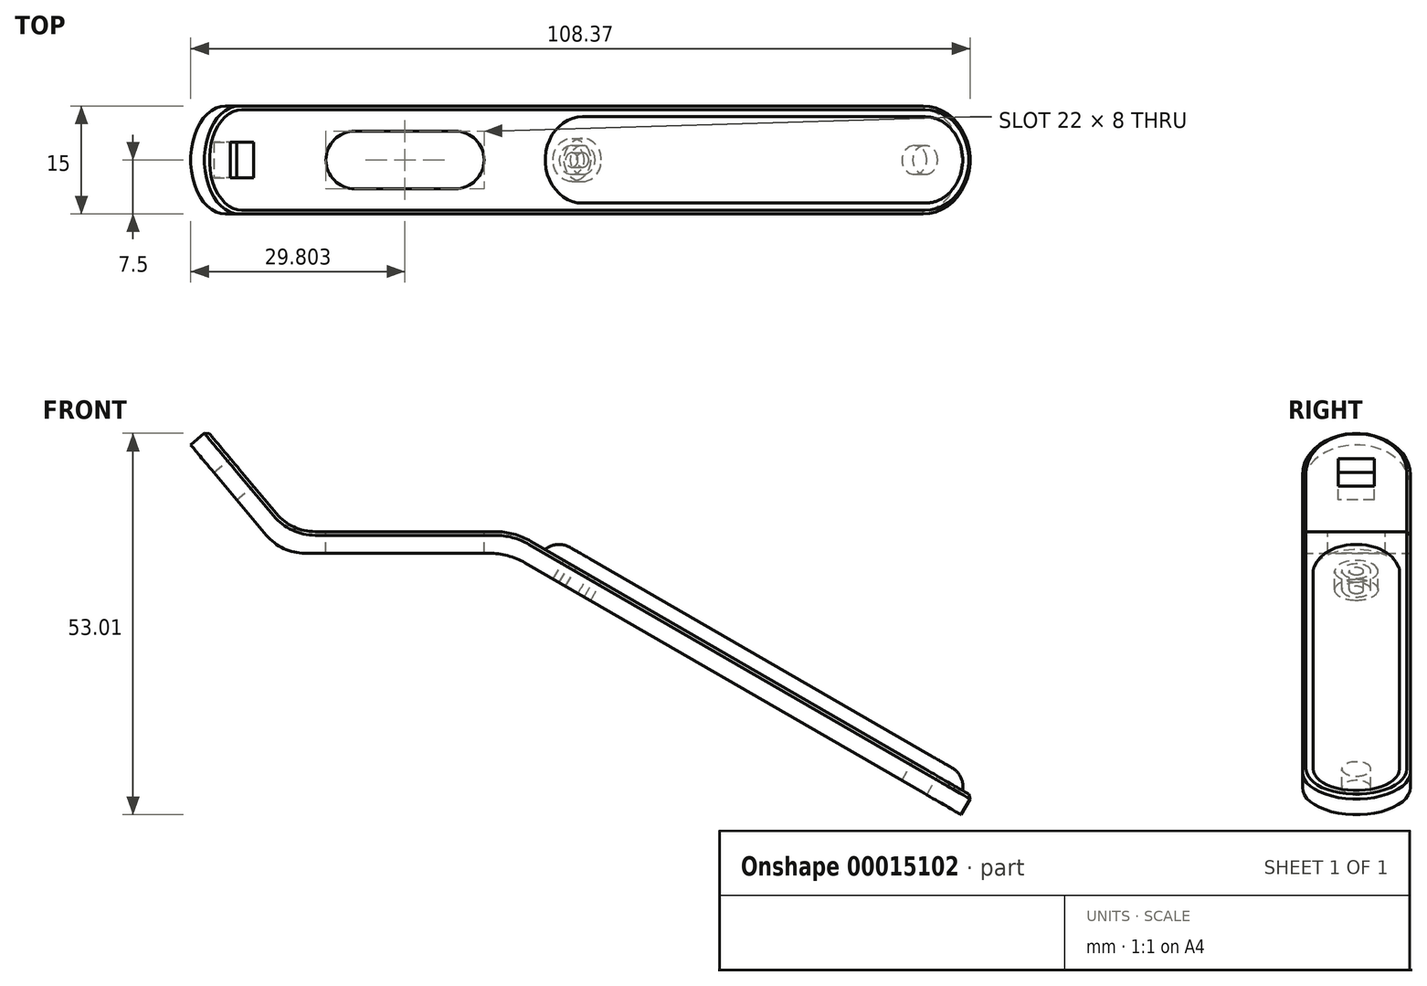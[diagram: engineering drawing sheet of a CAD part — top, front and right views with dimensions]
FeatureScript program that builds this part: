
annotation { "Feature Type Name" : "Feature", "Feature Type Description" : "" }
export const myFeature = defineFeature(function(context is Context, id is Id, definition is map)
    precondition{}
    {
        {
            var Q0;
            Q0=qCreatedBy(makeId("Front.planeOp"),FACE);
            var sketch = newSketch(context, id + "F0", { "sketchPlane" : qUnion([Q0])});
            skLineSegment(sketch, "E0.bottom", {"start": v(3.26, 0) * mm, "end": v(28.86, 0) * mm});
            skLineSegment(sketch, "E0.top", {"start": v(4.66, 3) * mm, "end": v(29.66, 3) * mm});
            skLineSegment(sketch, "E1", {"start": v(-0.7, 5.5) * mm, "end": v(-10.34, 17) * mm});
            skLineSegment(sketch, "E2", {"start": v(-10.34, 17) * mm, "end": v(-12.64, 15.06) * mm});
            skLineSegment(sketch, "E3", {"start": v(-12.64, 15.06) * mm, "end": v(-2.1, 2.5) * mm});
            skLineSegment(sketch, "E4", {"start": v(34.66, 1.66) * mm, "end": v(95.98, -33.74) * mm});
            skLineSegment(sketch, "E5", {"start": v(95.98, -33.74) * mm, "end": v(94.48, -36.34) * mm});
            skLineSegment(sketch, "E6", {"start": v(94.48, -36.34) * mm, "end": v(33.86, -1.34) * mm});
            skPoint(sketch, "E7.visualSharp", {"position": v(1.4, 3) * mm});
            skArc(sketch, "E7.filletArc", {"start": v(-0.7, 5.5) * mm, "mid": v(1.7, 3.66) * mm, "end": v(4.66, 3) * mm});
            skPoint(sketch, "E8.visualSharp", {"position": v(31.54, 0) * mm});
            skArc(sketch, "E8.filletArc", {"start": v(33.86, -1.34) * mm, "mid": v(31.45, -0.34) * mm, "end": v(28.86, 0) * mm});
            skPoint(sketch, "E9.visualSharp", {"position": v(32.34, 3) * mm});
            skArc(sketch, "E9.filletArc", {"start": v(34.66, 1.66) * mm, "mid": v(32.25, 2.66) * mm, "end": v(29.66, 3) * mm});
            skPoint(sketch, "E10.visualSharp", {"position": v(0, 0) * mm});
            skArc(sketch, "E10.filletArc", {"start": v(-2.1, 2.5) * mm, "mid": v(0.3, 0.66) * mm, "end": v(3.26, 0) * mm});
            skSolve(sketch);
        }
        {
            var Q0;
            Q0=makeQuery(id+"F0.imprint","IMPRINT",FACE,{"disambiguationData":[TD([[makeQuery(id+"F0.imprint","IMPRINT",EDGE,{"derivedFrom":sQuery(id+"F0.wireOp",EDGE,"E0.bottom")}),1.0]])]});
            extrude(context, id + "F1", {"entities" : qUnion([Q0]), "endBound" : BoundingType.SYMMETRIC, "depth" : 15 * mm});
        }
        {
            var Q0;
            Q0=makeQuery(id+"F1.opExtrude","CAP_EDGE",EDGE,{"disambiguationData":[OSD([sQuery(id+"F0.wireOp",EDGE,"E2")])],"isStart":false});
            var Q1;
            Q1=makeQuery(id+"F1.opExtrude","CAP_EDGE",EDGE,{"disambiguationData":[OSD([sQuery(id+"F0.wireOp",EDGE,"E2")])],"isStart":true});
            var Q2;
            Q2=makeQuery(id+"F1.opExtrude","CAP_EDGE",EDGE,{"disambiguationData":[OSD([sQuery(id+"F0.wireOp",EDGE,"E5")])],"isStart":false});
            var Q3;
            Q3=makeQuery(id+"F1.opExtrude","CAP_EDGE",EDGE,{"disambiguationData":[OSD([sQuery(id+"F0.wireOp",EDGE,"E5")])],"isStart":true});
            fillet(context, id + "F2", {"entities" : qUnion([Q0, Q1, Q2, Q3]), "radius" : 7.5 * mm, "tangentPropagation" : true, "allowEdgeOverflow" : false});
        }
        {
            var Q0;
            Q0=makeQuery(id+"F1.opExtrude","SWEPT_FACE",FACE,{"disambiguationData":[OSD([sQuery(id+"F0.wireOp",EDGE,"E1")])]});
            var sketch = newSketch(context, id + "F3", { "sketchPlane" : qUnion([Q0])});
            skArc(sketch, "E11.0", {"start": v(7.5, 12.16) * mm, "mid": v(0, 19.66) * mm, "end": v(-7.5, 12.16) * mm});
            skLineSegment(sketch, "E12.rect.bottom", {"start": v(2.5, 9.66) * mm, "end": v(-2.5, 9.66) * mm});
            skLineSegment(sketch, "E12.rect.top", {"start": v(2.5, 14.66) * mm, "end": v(-2.5, 14.66) * mm});
            skLineSegment(sketch, "E12.rect.left", {"start": v(2.5, 9.66) * mm, "end": v(2.5, 14.66) * mm});
            skLineSegment(sketch, "E12.rect.right", {"start": v(-2.5, 9.66) * mm, "end": v(-2.5, 14.66) * mm});
            skSolve(sketch);
        }
        {
            var Q0;
            Q0=makeQuery(id+"F3.imprint","IMPRINT",FACE,{"disambiguationData":[TD([[makeQuery(id+"F3.imprint","IMPRINT",EDGE,{"derivedFrom":sQuery(id+"F3.wireOp",EDGE,"E12.rect.bottom")}),-1.0]])]});
            extrude(context, id + "F4", {"entities" : qUnion([Q0]), "operationType" : NewBodyOperationType.REMOVE, "endBound" : BoundingType.THROUGH_ALL, "oppositeDirection" : true, "depth" : 25 * mm});
        }
        {
            var Q0;
            Q0=makeQuery(id+"F1.opExtrude","SWEPT_FACE",FACE,{"disambiguationData":[OSD([sQuery(id+"F0.wireOp",EDGE,"E4")])]});
            var sketch = newSketch(context, id + "F5", { "sketchPlane" : qUnion([Q0])});
            skArc(sketch, "E13.0", {"start": v(92.5, -7.5) * mm, "mid": v(100, 0) * mm, "end": v(92.5, 7.5) * mm});
            skLineSegment(sketch, "E14", {"start": v(92.5, 0) * mm, "end": v(29.19, 0) * mm, "construction": true});
            skCircle(sketch, "E15", {"center": v(92.5, 0) * mm, "radius": 3 * mm});
            skCircle(sketch, "E16", {"center": v(37.5, 0) * mm, "radius": 3 * mm});
            skSolve(sketch);
        }
        {
            var Q0;
            Q0=makeQuery(id+"F5.imprint","IMPRINT",FACE,{"disambiguationData":[TD([[makeQuery(id+"F5.imprint","IMPRINT",EDGE,{"derivedFrom":sQuery(id+"F5.wireOp",EDGE,"E16")}),1.0]])]});
            var Q1;
            Q1=makeQuery(id+"F5.imprint","IMPRINT",FACE,{"disambiguationData":[TD([[makeQuery(id+"F5.imprint","IMPRINT",EDGE,{"derivedFrom":sQuery(id+"F5.wireOp",EDGE,"E15")}),1.0]])]});
            extrude(context, id + "F6", {"entities" : qUnion([Q0, Q1]), "operationType" : NewBodyOperationType.REMOVE, "endBound" : BoundingType.THROUGH_ALL, "oppositeDirection" : true, "depth" : 25 * mm});
        }
        {
            var Q0;
            Q0=makeQuery(id+"F1.opExtrude","SWEPT_FACE",FACE,{"disambiguationData":[OSD([sQuery(id+"F0.wireOp",EDGE,"E0.top")])]});
            var sketch = newSketch(context, id + "F7", { "sketchPlane" : qUnion([Q0])});
            skLineSegment(sketch, "E17", {"start": v(4.66, 0) * mm, "end": v(29.66, 0) * mm, "construction": true});
            skArc(sketch, "E18", {"start": v(10.16, 4) * mm, "mid": v(6.16, 0) * mm, "end": v(10.16, -4) * mm});
            skArc(sketch, "E19", {"start": v(24.16, -4) * mm, "mid": v(28.16, 0) * mm, "end": v(24.16, 4) * mm});
            skLineSegment(sketch, "E20", {"start": v(17.16, 7.5) * mm, "end": v(17.16, -7.5) * mm, "construction": true});
            skLineSegment(sketch, "E21", {"start": v(10.16, 4) * mm, "end": v(24.16, 4) * mm});
            skLineSegment(sketch, "E22", {"start": v(24.16, -4) * mm, "end": v(10.16, -4) * mm});
            skSolve(sketch);
        }
        {
            var Q0;
            Q0=makeQuery(id+"F7.imprint","IMPRINT",FACE,{"disambiguationData":[TD([[makeQuery(id+"F7.imprint","IMPRINT",EDGE,{"derivedFrom":sQuery(id+"F7.wireOp",EDGE,"E18")}),1.0]])]});
            extrude(context, id + "F8", {"entities" : qUnion([Q0]), "operationType" : NewBodyOperationType.REMOVE, "endBound" : BoundingType.THROUGH_ALL, "oppositeDirection" : true, "depth" : 25 * mm});
        }
        {
            var Q0;
            Q0=makeQuery(id+"F1.opExtrude","CAP_EDGE",EDGE,{"disambiguationData":[OSD([sQuery(id+"F0.wireOp",EDGE,"E1")])],"isStart":false});
            var Q1;
            Q1=makeQuery(id+"F2.opFillet","BLEND_EDGE",EDGE,{"blendedFrom":[makeQuery(id+"F1.opExtrude","CAP_EDGE",EDGE,{"disambiguationData":[OSD([sQuery(id+"F0.wireOp",EDGE,"E2")])],"isStart":false}),makeQuery(id+"F1.opExtrude","SWEPT_FACE",FACE,{"disambiguationData":[OSD([sQuery(id+"F0.wireOp",EDGE,"E3")])]})],"blendedInto":[makeQuery(id+"F1.opExtrude","SWEPT_FACE",FACE,{"disambiguationData":[OSD([sQuery(id+"F0.wireOp",EDGE,"E3")])]})]});
            chamfer(context, id + "F9", {"entities" : qUnion([Q0, Q1]), "width" : .5 * mm, "tangentPropagation" : true});
        }
        {
            var Q0;
            Q0=makeQuery(id+"F1.opExtrude","SWEPT_FACE",FACE,{"disambiguationData":[OSD([sQuery(id+"F0.wireOp",EDGE,"E4")])]});
            var sketch = newSketch(context, id + "F10", { "sketchPlane" : qUnion([Q0])});
            skCircle(sketch, "E23.0", {"center": v(37.5, 0) * mm, "radius": 3 * mm, "construction": true});
            skCircle(sketch, "E24.0", {"center": v(92.5, 0) * mm, "radius": 3 * mm});
            skCircle(sketch, "E25", {"center": v(37.5, 0) * mm, "radius": 2 * mm});
            skArc(sketch, "E26", {"start": v(92.5, -6) * mm, "mid": v(98.5, 0) * mm, "end": v(92.5, 6) * mm});
            skArc(sketch, "E27", {"start": v(37.5, 6) * mm, "mid": v(31.5, 0) * mm, "end": v(37.5, -6) * mm});
            skLineSegment(sketch, "E28", {"start": v(37.5, -6) * mm, "end": v(92.5, -6) * mm});
            skLineSegment(sketch, "E29", {"start": v(92.5, 6) * mm, "end": v(37.5, 6) * mm});
            skCircle(sketch, "E30", {"center": v(92.5, 0) * mm, "radius": 2 * mm});
            skCircle(sketch, "E31", {"center": v(37.5, 0) * mm, "radius": 1 * mm});
            skSolve(sketch);
        }
        {
            var Q0;
            Q0=makeQuery(id+"F10.imprint","IMPRINT",FACE,{"disambiguationData":[TD([[makeQuery(id+"F10.imprint","IMPRINT",EDGE,{"derivedFrom":sQuery(id+"F10.wireOp",EDGE,"E24.0")}),-1.0]])]});
            var Q1;
            Q1=makeQuery(id+"F10.imprint","IMPRINT",FACE,{"disambiguationData":[TD([[makeQuery(id+"F10.imprint","IMPRINT",EDGE,{"derivedFrom":sQuery(id+"F10.wireOp",EDGE,"E25")}),-1.0]])]});
            var Q2;
            Q2=makeQuery(id+"F10.imprint","IMPRINT",FACE,{"disambiguationData":[TD([[makeQuery(id+"F10.imprint","IMPRINT",EDGE,{"derivedFrom":sQuery(id+"F10.wireOp",EDGE,"E25")}),1.0]])]});
            var Q3;
            Q3=makeQuery(id+"F10.imprint","IMPRINT",FACE,{"disambiguationData":[TD([[makeQuery(id+"F10.imprint","IMPRINT",EDGE,{"derivedFrom":sQuery(id+"F10.wireOp",EDGE,"E31")}),1.0]])]});
            var Q4;
            Q4=makeQuery(id+"F10.imprint","IMPRINT",FACE,{"disambiguationData":[TD([[makeQuery(id+"F10.imprint","IMPRINT",EDGE,{"derivedFrom":sQuery(id+"F10.wireOp",EDGE,"E24.0")}),1.0]])]});
            var Q5;
            Q5=makeQuery(id+"F10.imprint","IMPRINT",FACE,{"disambiguationData":[TD([[makeQuery(id+"F10.imprint","IMPRINT",EDGE,{"derivedFrom":sQuery(id+"F10.wireOp",EDGE,"E30")}),1.0]])]});
            extrude(context, id + "F11", {"entities" : qUnion([Q0, Q1, Q2, Q3, Q4, Q5]), "depth" : 2 * mm});
        }
        {
            var Q0;
            Q0=makeQuery(id+"F10.imprint","IMPRINT",FACE,{"disambiguationData":[TD([[makeQuery(id+"F10.imprint","IMPRINT",EDGE,{"derivedFrom":sQuery(id+"F10.wireOp",EDGE,"E24.0")}),1.0]])]});
            var Q1;
            Q1=makeQuery(id+"F10.imprint","IMPRINT",FACE,{"disambiguationData":[TD([[makeQuery(id+"F10.imprint","IMPRINT",EDGE,{"derivedFrom":sQuery(id+"F10.wireOp",EDGE,"E25")}),1.0]])]});
            extrude(context, id + "F12", {"entities" : qUnion([Q0, Q1]), "operationType" : NewBodyOperationType.ADD, "oppositeDirection" : true, "depth" : 3 * mm});
        }
        {
            var Q0;
            Q0=makeQuery(id+"F11.opExtrude","CAP_EDGE",EDGE,{"disambiguationData":[OSD([sQuery(id+"F10.wireOp",EDGE,"E28")])],"isStart":false});
            fillet(context, id + "F13", {"entities" : qUnion([Q0]), "radius" : 3 * mm, "tangentPropagation" : true, "allowEdgeOverflow" : false});
        }
    });
